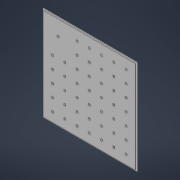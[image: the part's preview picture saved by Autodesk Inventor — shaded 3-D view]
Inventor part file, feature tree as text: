
AUTODESK INVENTOR PART (.ipt)
format: ipt  version: 2022 (Build 260153000, 153)  size: 172,032 bytes
history: native  units: mm
features: sketch x6, extrude x5, pattern_linear x2
ambient origin geometry x8: Origin, YZ Plane, XZ Plane, XY Plane, X Axis, Y Axis, Z Axis, Center Point
bodies: Solid1 (feature_tree)
feature tree (13):
  extrude  "Extrusion1"  Depth=220.0mm
  extrude  "Extrusion2"  Depth=214.0mm
  extrude  "Extrusion3"  Depth=220.0mm
  pattern_linear  "Rectangular Pattern1"  Count1=22  [1 undecoded]
  extrude  "Extrusion4"  Depth=1.5mm
  pattern_linear  "Rectangular Pattern2"  Count1=20  [1 undecoded]
  extrude  "Extrusion5"  Depth=28.5mm
  sketch  "Sketch7"  dims[d14=5.0mm d15=3.0mm d16=0.0mm d17=50.0mm d19=28.5mm d20=70.0mm d22=28.5mm d23=28.5mm d24=5.0mm d25=3.0mm d26=0.0mm d27=50.0mm d29=28.5mm d30=20.0mm d32=28.5mm d33=200.0mm d34=200.0mm d35=55.0mm d36=55.0mm d37=5.0mm d38=3.0mm d39=0.0mm]
  sketch  "Sketch2"  dims[d0=220.0mm d1=220.0mm]
  sketch  "Sketch3"  dims[d2=3.0mm d3=0.0mm d4=214.0mm]
  sketch  "Sketch4"  dims[d5=214.0mm d6=220.0mm d7=220.0mm]
  sketch  "Sketch5"  dims[d8=1.5mm d9=0.0mm d10=200.0mm d11=200.0mm]
  sketch  "Sketch6"  dims[d12=28.5mm d13=28.5mm]
note: 2 required parameter values undecoded (feature->parameter linkage not recoverable at this tier; creation-order binding heuristic only, values carry confidence <= 0.55)
